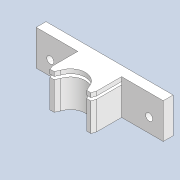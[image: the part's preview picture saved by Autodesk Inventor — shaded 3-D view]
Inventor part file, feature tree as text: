
AUTODESK INVENTOR PART (.ipt)
format: ipt  version: 2020 (Build 240168000, 168)  size: 184,832 bytes
history: native  units: mm
features: extrude x5, sketch x5, chamfer x4, reference x2, other x2, mirror x1, hole x1, projected_geometry x1
ambient origin geometry x8: Origin, YZ Plane, XZ Plane, XY Plane, X Axis, Y Axis, Z Axis, Center Point
bodies: Solid1 (feature_tree)
feature tree (21):
  extrude  "Extrusion1"  Depth=90.0mm
  extrude  "Extrusion2"  Depth=20.75mm
  mirror  "Mirror1"
  extrude  "Extrusion3"  TaperAngle=0.0deg  [1 undecoded]
  chamfer  "Chamfer1"  Distance=3.0mm Angle=45.0deg
  chamfer  "Chamfer2"  Distance=3.0mm Angle=45.0deg
  hole  "Hole1"  [1 undecoded]
  chamfer  "Chamfer3"  Distance=21.1mm
  chamfer  "Chamfer4"  Distance=3.0mm Angle=45.0deg
  extrude  "Extrusion4"  Depth=3.0mm TaperAngle=45.0deg
  extrude  "Extrusion5"  TaperAngle=0.0deg  [1 undecoded]
  sketch  "Sketch1"  dims[d0=20.0mm d1=90.0mm]
  sketch  "Sketch3"  dims[d2=27.75mm d3=0.0mm d8=20.75mm]
  sketch  "Sketch5"  dims[d9=0.0mm d10=0.0mm d11=0.0mm d12=0.0mm d13=1.0mm d14=3.0mm d15=45.0deg d16=1.0mm d17=3.0mm d18=45.0deg]
  reference  "Reference5"
  sketch  "Sketch6"  dims[d20=15.5mm d23=70.0mm]
  projected_geometry  "Projected Loop1"
  sketch  "Sketch7"  dims[d24=5.0mm d25=6.0mm d26=4.0mm d27=2.0mm d28=90.0deg d29=8.0mm d30=20.594885mm d32=21.1mm d33=1.0mm d34=3.0mm d35=45.0deg d36=1.0mm d37=3.0mm d38=45.0deg d39=0.0mm d40=7.0mm d41=5.0mm d42=0.0mm d43=2.0mm d44=17.75mm d45=0.0mm]
  reference  "Reference8"
  other  "0008-10-10 Injectomat Standard_Seringa 20.iam"
  other  "0008-10-002 Corp_Injectomat1.ipt:10"
note: 3 required parameter values undecoded (feature->parameter linkage not recoverable at this tier; creation-order binding heuristic only, values carry confidence <= 0.55)
